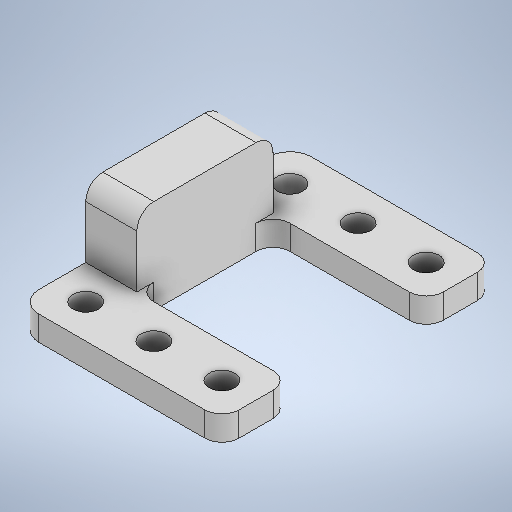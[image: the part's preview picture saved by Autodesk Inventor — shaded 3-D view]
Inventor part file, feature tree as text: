
AUTODESK INVENTOR PART (.ipt)
format: ipt  version: 2025.1 (Build 291241020, 241B)  size: 399,360 bytes
history: native  units: in
note: dims shown in document units (in); Inventor stores cm internally (conversion verified against a paired STEP export)
features: extrude x13, sketch x13, projected_geometry x4, fillet x3
ambient origin geometry x8: Origin, YZ Plane, XZ Plane, XY Plane, X Axis, Y Axis, Z Axis, Center Point
bodies: Solid1 (feature_tree)
feature tree (33):
  extrude  "Extrusion1"  Depth=0.36in
  sketch  "Sketch2"  dims[d2=2.5in d3=0.0in d4=0.25in]
  extrude  "Extrusion2"  Depth=0.25in
  extrude  "Extrusion3"  Depth=1.0in
  extrude  "Extrusion4"  Depth=0.375in
  extrude  "Extrusion5"  Depth=0.125in TaperAngle=0.0deg
  extrude  "Extrusion8"  Depth=1.0in TaperAngle=0.0deg
  extrude  "Extrusion9"  Depth=0.625in
  extrude  "Extrusion10"  Depth=2.0in TaperAngle=0.0deg
  extrude  "Extrusion11"  Depth=1.385in TaperAngle=0.0deg
  extrude  "Extrusion12"  Depth=1.0in
  extrude  "Extrusion13"  Depth=3.0in
  fillet  "Fillet2"  Radius=3.0in
  extrude  "Extrusion14"  Depth=0.375in
  fillet  "Fillet3"  Radius=0.375in
  extrude  "Extrusion15"  Depth=0.3125in
  fillet  "Fillet5"  Radius=1.025in
  sketch  "Sketch1"  dims[d0=1.0in d1=0.36in]
  sketch  "Sketch3"  dims[d5=1.0in d6=1.0in]
  sketch  "Sketch4"  dims[d7=0.375in d8=0.375in]
  projected_geometry  "Projected Loop1"
  sketch  "Sketch5"  dims[d9=0.375in d10=0.125in d11=0.0in]
  projected_geometry  "Projected Loop2"
  sketch  "Sketch8"  dims[d13=1.0in d14=0.0in d15=0.2in d16=0.0in]
  sketch  "Sketch9"  dims[d17=0.05in d18=0.0in d24=0.625in]
  projected_geometry  "Projected Loop4"
  sketch  "Sketch10"  dims[d25=2.0in d26=0.0in d27=0.125in d28=0.0in]
  sketch  "Sketch11"  dims[d29=0.375in d34=1.385in d35=0.0in]
  projected_geometry  "Projected Loop5"
  sketch  "Sketch13"  dims[d36=1.0in d37=0.0in d38=1.0in]
  sketch  "Sketch14"  dims[d39=2.25in d40=0.0in d42=3.0in d43=3.0in]
  sketch  "Sketch15"  dims[d44=0.375in d45=0.375in d46=0.375in]
  sketch  "Sketch16"  dims[d47=0.8125in d48=0.0in d49=0.3125in d50=1.025in d51=0.0in d52=0.25in d55=0.375in d56=0.375in d58=0.865in d59=0.0in d60=0.25in]
